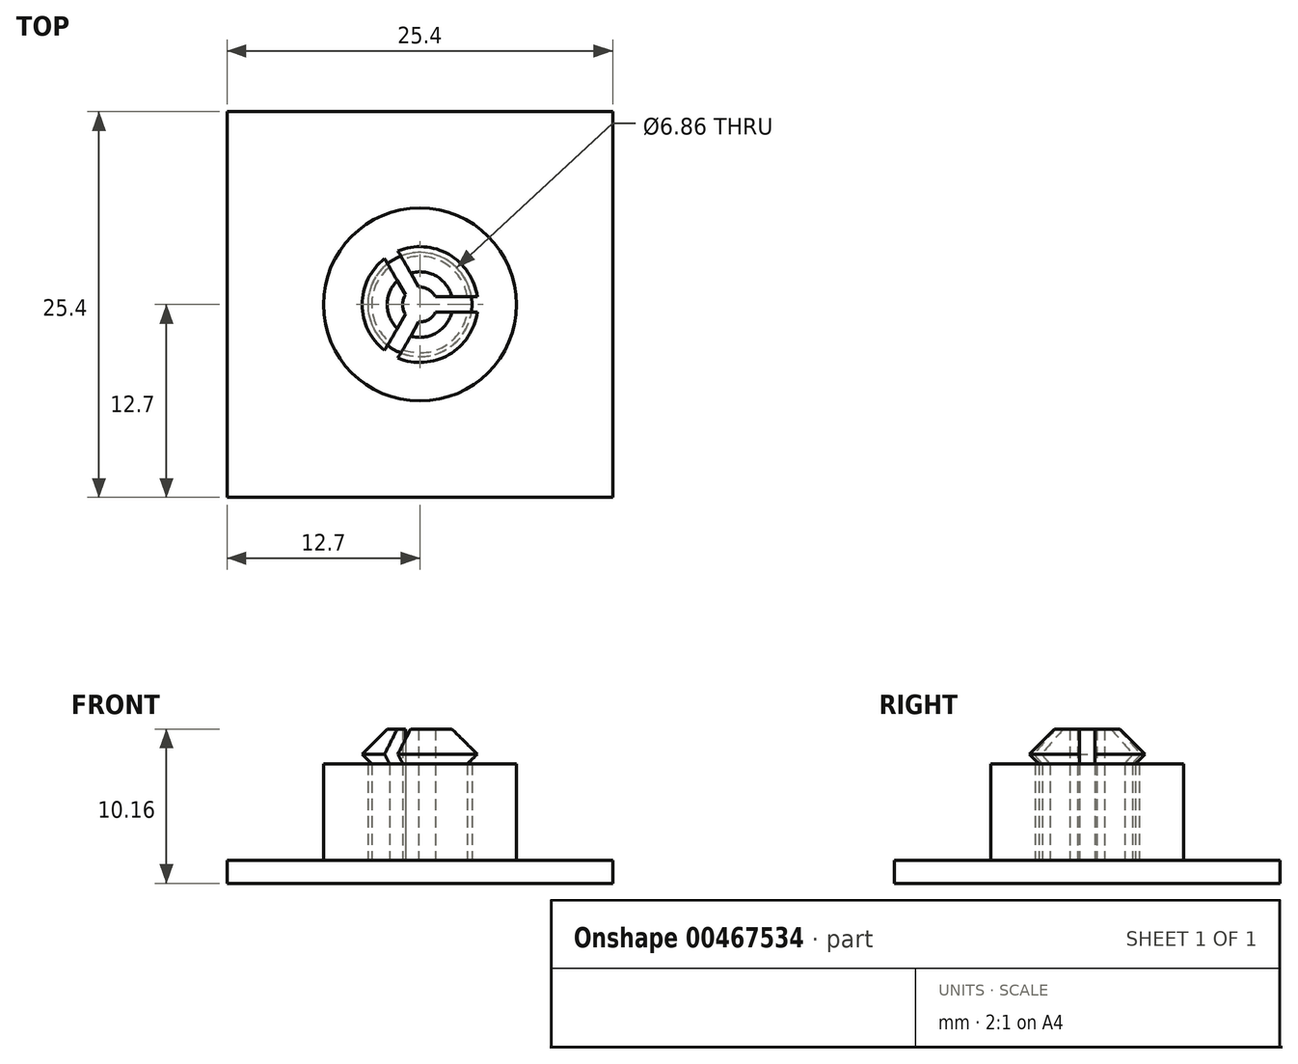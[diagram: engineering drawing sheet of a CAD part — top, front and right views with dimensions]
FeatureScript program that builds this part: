
annotation { "Feature Type Name" : "Feature", "Feature Type Description" : "" }
export const myFeature = defineFeature(function(context is Context, id is Id, definition is map)
    precondition{}
    {
        {
            var Q0;
            Q0=qCreatedBy(makeId("Top.planeOp"),FACE);
            var sketch = newSketch(context, id + "F0", { "sketchPlane" : qUnion([Q0])});
            skLineSegment(sketch, "E0.bottom", {"start": v(12.7, 12.7) * mm, "end": v(-12.7, 12.7) * mm});
            skLineSegment(sketch, "E0.top", {"start": v(12.7, -12.7) * mm, "end": v(-12.7, -12.7) * mm});
            skLineSegment(sketch, "E0.left", {"start": v(12.7, 12.7) * mm, "end": v(12.7, -12.7) * mm});
            skLineSegment(sketch, "E0.right", {"start": v(-12.7, 12.7) * mm, "end": v(-12.7, -12.7) * mm});
            skPoint(sketch, "E0.middle", {"position": v(0, 0) * mm});
            skSolve(sketch);
        }
        {
            var Q0;
            Q0=makeQuery(id+"F0.imprint","IMPRINT",FACE,{"disambiguationData":[TD([[makeQuery(id+"F0.imprint","IMPRINT",EDGE,{"derivedFrom":sQuery(id+"F0.wireOp",EDGE,"E0.bottom")}),1.0]])]});
            extrude(context, id + "F1", {"entities" : qUnion([Q0]), "depth" : 1.52 * mm});
        }
        {
            var Q0;
            Q0=qCreatedBy(makeId("Front.planeOp"),FACE);
            var sketch = newSketch(context, id + "F2", { "sketchPlane" : qUnion([Q0])});
            skLineSegment(sketch, "E1", {"start": v(0, 0) * mm, "end": v(3.18, 0) * mm});
            skLineSegment(sketch, "E2", {"start": v(3.18, 0) * mm, "end": v(3.18, 7.87) * mm});
            skLineSegment(sketch, "E3", {"start": v(3.17, 7.87) * mm, "end": v(3.81, 8.5) * mm});
            skLineSegment(sketch, "E4", {"start": v(3.81, 8.5) * mm, "end": v(2.16, 10.16) * mm});
            skLineSegment(sketch, "E5", {"start": v(2.16, 10.16) * mm, "end": v(1.14, 10.16) * mm});
            skLineSegment(sketch, "E6", {"start": v(1.14, 10.16) * mm, "end": v(1.14, 0) * mm});
            skLineSegment(sketch, "E7", {"start": v(0, 0) * mm, "end": v(0, 15.43) * mm});
            skSolve(sketch);
        }
        {
            var Q0;
            {var subQ0=sQuery(id+"F2.wireOp",EDGE,"E2");Q0=makeQuery(id+"F2.imprint","IMPRINT",FACE,{"disambiguationData":[TD([[makeQuery(id+"F2.imprint","IMPRINT",EDGE,{"derivedFrom":subQ0}),1.0]])]});}
            var Q1;
            Q1=sQuery(id+"F2.wireOp",EDGE,"E7");
            revolve(context, id + "F3", {"operationType" : NewBodyOperationType.ADD, "entities" : qUnion([Q0]), "axis" : qUnion([Q1]), "revolveType" : RevolveType.FULL});
        }
        {
            var Q0;
            Q0=makeQuery(id+"F3.opRevolve","SWEPT_FACE",FACE,{"disambiguationData":[OSD([sQuery(id+"F2.wireOp",EDGE,"E5")])]});
            var sketch = newSketch(context, id + "F4", { "sketchPlane" : qUnion([Q0])});
            skLineSegment(sketch, "E8", {"start": v(0, 0) * mm, "end": v(6.35, 0) * mm, "construction": true});
            skPoint(sketch, "E9.center", {"position": v(0, 0) * mm});
            skLineSegment(sketch, "E10.0", {"start": v(0.3, -0.5) * mm, "end": v(6.35, -0.5) * mm});
            skLineSegment(sketch, "E11", {"start": v(0, 0) * mm, "end": v(-3.17, -5.5) * mm, "construction": true});
            skLineSegment(sketch, "E12", {"start": v(0, 0) * mm, "end": v(-3.18, 5.5) * mm, "construction": true});
            skLineSegment(sketch, "E13.0", {"start": v(0.3, 0.5) * mm, "end": v(6.35, 0.5) * mm});
            skLineSegment(sketch, "E14.0", {"start": v(0.3, -0.5) * mm, "end": v(-2.74, -5.75) * mm});
            skLineSegment(sketch, "E15.0", {"start": v(-0.59, 0) * mm, "end": v(-3.61, -5.25) * mm});
            skLineSegment(sketch, "E16.0", {"start": v(0.3, 0.5) * mm, "end": v(-2.74, 5.75) * mm});
            skLineSegment(sketch, "E17.0", {"start": v(-0.59, 0) * mm, "end": v(-3.61, 5.25) * mm});
            skLineSegment(sketch, "E18", {"start": v(6.35, 0.5) * mm, "end": v(6.35, -0.5) * mm});
            skLineSegment(sketch, "E19", {"start": v(-2.74, -5.75) * mm, "end": v(-3.61, -5.25) * mm});
            skLineSegment(sketch, "E20", {"start": v(-3.61, 5.25) * mm, "end": v(-2.74, 5.75) * mm});
            skSolve(sketch);
        }
        {
            var Q0;
            {var subQ0=sQuery(id+"F4.wireOp",EDGE,"E18");Q0=makeQuery(id+"F4.imprint","IMPRINT",FACE,{"disambiguationData":[TD([[makeQuery(id+"F4.imprint","IMPRINT",EDGE,{"derivedFrom":subQ0}),-1.0]])]});}
            var Q1;
            {var subQ0=sQuery(id+"F4.wireOp",EDGE,"E10.0");var subQ1=sQuery(id+"F2.wireOp",EDGE,"E5");var subQ2=makeQuery(id+"F3.opRevolve","SWEPT_EDGE",EDGE,{"disambiguationData":[OSD([sQuery(id+"F2.wireOp",EDGE,"E4"),subQ1])]});var subQ3=makeQuery(id+"F4.imprint","INTERSECT",VERTEX,{"derivedFrom":[subQ2,subQ0]});Q1=makeQuery(id+"F4.imprint","IMPRINT",FACE,{"disambiguationData":[TD([[makeQuery(id+"F4.imprint","IMPRINT",EDGE,{"disambiguationData":[TD([[subQ3,1.0]])],"derivedFrom":subQ0}),1.0]])]});}
            var Q2;
            {var subQ5=sQuery(id+"F4.wireOp",EDGE,"E14.0");var subQ6=sQuery(id+"F4.wireOp",EDGE,"E10.0");var subQ7=makeQuery(id+"F4.imprint","INTERSECT",VERTEX,{"derivedFrom":[subQ6,subQ5]});Q2=makeQuery(id+"F4.imprint","IMPRINT",FACE,{"disambiguationData":[TD([[makeQuery(id+"F4.imprint","IMPRINT",EDGE,{"disambiguationData":[TD([[subQ7,-1.0]])],"derivedFrom":subQ6}),1.0]])]});}
            var Q3;
            {var subQ0=sQuery(id+"F4.wireOp",EDGE,"E14.0");var subQ1=sQuery(id+"F2.wireOp",EDGE,"E5");var subQ2=makeQuery(id+"F3.opRevolve","SWEPT_EDGE",EDGE,{"disambiguationData":[OSD([sQuery(id+"F2.wireOp",EDGE,"E4"),subQ1])]});var subQ3=makeQuery(id+"F4.imprint","INTERSECT",VERTEX,{"derivedFrom":[subQ2,subQ0]});Q3=makeQuery(id+"F4.imprint","IMPRINT",FACE,{"disambiguationData":[TD([[makeQuery(id+"F4.imprint","IMPRINT",EDGE,{"disambiguationData":[TD([[subQ3,1.0]])],"derivedFrom":subQ0}),-1.0]])]});}
            var Q4;
            {var subQ0=sQuery(id+"F4.wireOp",EDGE,"E19");Q4=makeQuery(id+"F4.imprint","IMPRINT",FACE,{"disambiguationData":[TD([[makeQuery(id+"F4.imprint","IMPRINT",EDGE,{"derivedFrom":subQ0}),-1.0]])]});}
            var Q5;
            {var subQ0=sQuery(id+"F4.wireOp",EDGE,"E20");Q5=makeQuery(id+"F4.imprint","IMPRINT",FACE,{"disambiguationData":[TD([[makeQuery(id+"F4.imprint","IMPRINT",EDGE,{"derivedFrom":subQ0}),-1.0]])]});}
            var Q6;
            {var subQ0=sQuery(id+"F4.wireOp",EDGE,"E16.0");var subQ1=sQuery(id+"F2.wireOp",EDGE,"E5");var subQ2=makeQuery(id+"F3.opRevolve","SWEPT_EDGE",EDGE,{"disambiguationData":[OSD([sQuery(id+"F2.wireOp",EDGE,"E4"),subQ1])]});var subQ3=makeQuery(id+"F4.imprint","INTERSECT",VERTEX,{"derivedFrom":[subQ2,subQ0]});Q6=makeQuery(id+"F4.imprint","IMPRINT",FACE,{"disambiguationData":[TD([[makeQuery(id+"F4.imprint","IMPRINT",EDGE,{"disambiguationData":[TD([[subQ3,1.0]])],"derivedFrom":subQ0}),1.0]])]});}
            var Q7;
            Q7=sQuery(id+"F4.wireOp",EDGE,"E13.0");
            var Q8;
            {var subQ0=sQuery(id+"F0.wireOp",EDGE,"E0.left");var subQ1=sQuery(id+"F0.wireOp",EDGE,"E0.top");var subQ2=sQuery(id+"F0.wireOp",EDGE,"E0.right");var subQ3=sQuery(id+"F0.wireOp",EDGE,"E0.bottom");Q8=makeQuery(id+"F3.boolean.opBoolean","SPLIT",FACE,{"disambiguationData":[TD([makeQuery(id+"F1.opExtrude","SWEPT_FACE",FACE,{"disambiguationData":[OSD([subQ3])]})])],"derivedFrom":makeQuery(id+"F1.opExtrude","CAP_FACE",FACE,{"disambiguationData":[OSD([subQ3,subQ1,subQ0,subQ2])],"isStart":false})});}
            extrude(context, id + "F5", {"entities" : qUnion([Q0, Q1, Q2, Q3, Q4, Q5, Q6]), "operationType" : NewBodyOperationType.REMOVE, "surfaceEntities" : qUnion([Q7]), "endBound" : BoundingType.UP_TO_SURFACE, "oppositeDirection" : true, "endBoundEntityFace" : qUnion([Q8]), "depth" : 25.4 * mm});
        }
        {
            var Q0;
            {var subQ0=sQuery(id+"F0.wireOp",EDGE,"E0.left");var subQ1=sQuery(id+"F0.wireOp",EDGE,"E0.top");var subQ2=sQuery(id+"F0.wireOp",EDGE,"E0.right");var subQ3=sQuery(id+"F0.wireOp",EDGE,"E0.bottom");var subQ4=makeQuery(id+"F1.opExtrude","CAP_FACE",FACE,{"disambiguationData":[OSD([subQ3,subQ1,subQ0,subQ2])],"isStart":false});Q0=makeQuery(id+"F5.boolean.opBoolean","MERGE",FACE,{"derivedFrom":[makeQuery(id+"F3.boolean.opBoolean","SPLIT",FACE,{"disambiguationData":[TD([makeQuery(id+"F3.opRevolve","SWEPT_FACE",FACE,{"disambiguationData":[OSD([sQuery(id+"F2.wireOp",EDGE,"E6")])]})])],"derivedFrom":subQ4}),makeQuery(id+"F3.boolean.opBoolean","SPLIT",FACE,{"disambiguationData":[TD([makeQuery(id+"F1.opExtrude","SWEPT_FACE",FACE,{"disambiguationData":[OSD([subQ3])]})])],"derivedFrom":subQ4}),makeQuery(id+"F5.opExtrude","CAP_FACE",FACE,{"disambiguationData":[OSD([sQuery(id+"F4.wireOp",EDGE,"E10.0"),sQuery(id+"F4.wireOp",EDGE,"E13.0"),sQuery(id+"F4.wireOp",EDGE,"E14.0"),sQuery(id+"F4.wireOp",EDGE,"E15.0"),sQuery(id+"F4.wireOp",EDGE,"E16.0"),sQuery(id+"F4.wireOp",EDGE,"E17.0"),sQuery(id+"F4.wireOp",EDGE,"E18"),sQuery(id+"F4.wireOp",EDGE,"E19"),sQuery(id+"F4.wireOp",EDGE,"E20")])],"isStart":false})]});}
            var sketch = newSketch(context, id + "F6", { "sketchPlane" : qUnion([Q0])});
            skCircle(sketch, "E21", {"center": v(0, 0) * mm, "radius": 3.43 * mm});
            skCircle(sketch, "E22", {"center": v(0, 0) * mm, "radius": 6.35 * mm});
            skSolve(sketch);
        }
        {
            var Q0;
            Q0=makeQuery(id+"F6.imprint","IMPRINT",FACE,{"disambiguationData":[TD([[makeQuery(id+"F6.imprint","IMPRINT",EDGE,{"derivedFrom":sQuery(id+"F6.wireOp",EDGE,"E21")}),-1.0]])]});
            extrude(context, id + "F7", {"entities" : qUnion([Q0]), "depth" : 6.35 * mm});
        }
    });
